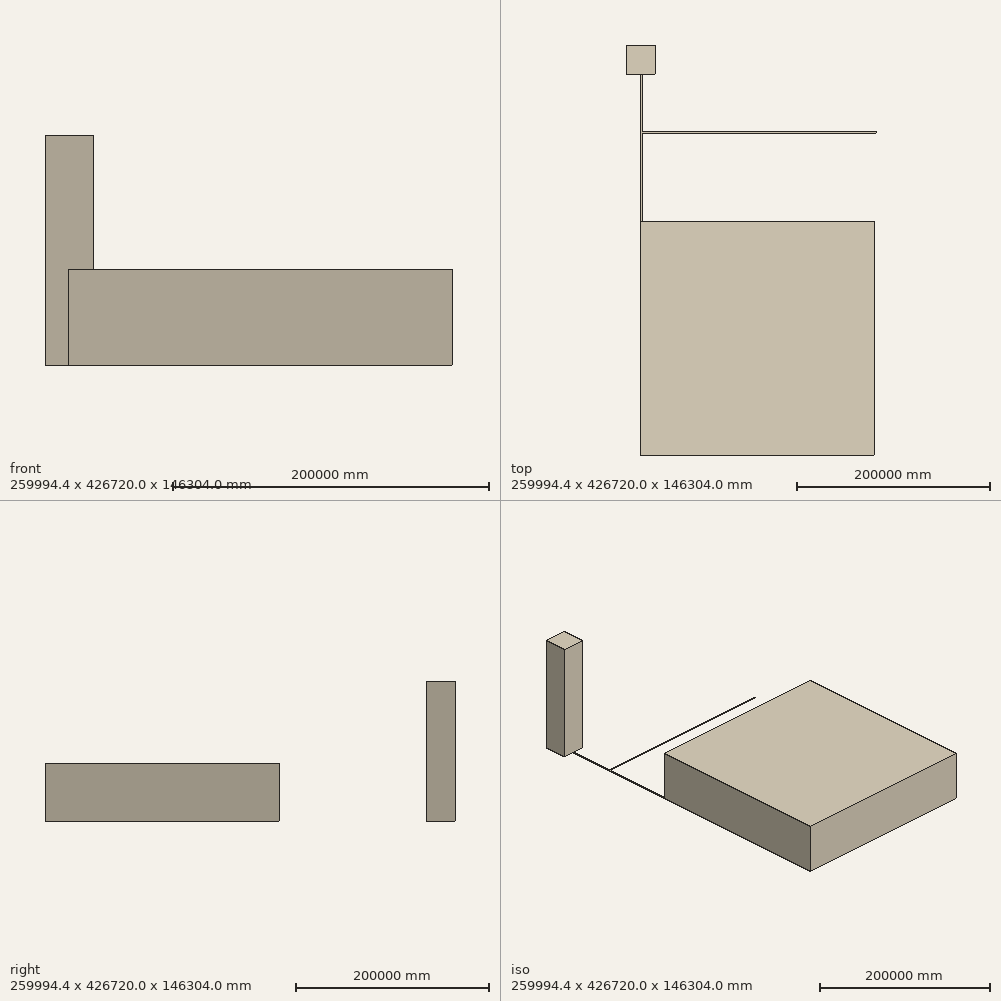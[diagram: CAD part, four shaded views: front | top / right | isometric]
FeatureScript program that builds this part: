
annotation { "Feature Type Name" : "Feature", "Feature Type Description" : "" }
export const myFeature = defineFeature(function(context is Context, id is Id, definition is map)
    precondition{}
    {
        {
            var Q0;
            Q0=qCreatedBy(makeId("Top.planeOp"),FACE);
            var sketch = newSketch(context, id + "F0", { "sketchPlane" : qUnion([Q0])});
            skLineSegment(sketch, "E0.bottom", {"start": v(15240, -15240) * mm, "end": v(-15240, -15240) * mm});
            skLineSegment(sketch, "E0.top", {"start": v(15240, 15240) * mm, "end": v(-15240, 15240) * mm});
            skLineSegment(sketch, "E0.left", {"start": v(15240, -15240) * mm, "end": v(15240, 15240) * mm});
            skLineSegment(sketch, "E0.right", {"start": v(-15240, -15240) * mm, "end": v(-15240, 15240) * mm});
            skPoint(sketch, "E0.middle", {"position": v(0, 0) * mm});
            skLineSegment(sketch, "E1.bottom", {"start": v(-914.4, -15240) * mm, "end": v(914.4, -15240) * mm});
            skLineSegment(sketch, "E1.left", {"start": v(-914.4, -15240) * mm, "end": v(-914.4, -167640) * mm});
            skLineSegment(sketch, "E1.right", {"start": v(914.4, -15240) * mm, "end": v(914.4, -167640) * mm});
            skLineSegment(sketch, "E2.bottom", {"start": v(914.4, -167640) * mm, "end": v(242925.6, -167640) * mm});
            skLineSegment(sketch, "E2.top", {"start": v(-914.4, -411480) * mm, "end": v(242925.6, -411480) * mm});
            skLineSegment(sketch, "E2.left", {"start": v(-914.4, -167640) * mm, "end": v(-914.4, -411480) * mm});
            skLineSegment(sketch, "E2.right", {"start": v(242925.6, -167640) * mm, "end": v(242925.6, -411480) * mm});
            skLineSegment(sketch, "E3", {"start": v(-914.4, -167640) * mm, "end": v(914.4, -167640) * mm});
            skLineSegment(sketch, "E4.bottom", {"start": v(914.4, -74152.27) * mm, "end": v(244754.4, -74152.27) * mm});
            skLineSegment(sketch, "E4.top", {"start": v(914.4, -75981.07) * mm, "end": v(244754.4, -75981.07) * mm});
            skLineSegment(sketch, "E4.left", {"start": v(914.4, -74152.27) * mm, "end": v(914.4, -75981.07) * mm});
            skLineSegment(sketch, "E4.right", {"start": v(244754.4, -74152.27) * mm, "end": v(244754.4, -75981.07) * mm});
            skSolve(sketch);
        }
        {
            var Q0;
            Q0=makeQuery(id+"F0.imprint","IMPRINT",FACE,{"disambiguationData":[TD([[makeQuery(id+"F0.imprint","IMPRINT",EDGE,{"derivedFrom":sQuery(id+"F0.wireOp",EDGE,"E0.top")}),1.0]])]});
            extrude(context, id + "F1", {"entities" : qUnion([Q0]), "depth" : 146304 * mm, "offsetDistance" : 25.4 * mm});
        }
        {
            var Q0;
            {var subQ2=sQuery(id+"F0.wireOp",EDGE,"E4.bottom");Q0=makeQuery(id+"F0.imprint","IMPRINT",FACE,{"disambiguationData":[TD([[makeQuery(id+"F0.imprint","IMPRINT",EDGE,{"derivedFrom":subQ2}),-1.0]])]});}
            var Q1;
            {var subQ4=sQuery(id+"F0.wireOp",EDGE,"E1.left");Q1=makeQuery(id+"F0.imprint","IMPRINT",FACE,{"disambiguationData":[TD([[makeQuery(id+"F0.imprint","IMPRINT",EDGE,{"derivedFrom":subQ4}),1.0]])]});}
            extrude(context, id + "F2", {"entities" : qUnion([Q0, Q1]), "operationType" : NewBodyOperationType.ADD, "depth" : 50.8 * mm, "offsetDistance" : 25.4 * mm});
        }
        {
            var Q0;
            Q0=makeQuery(id+"F0.imprint","IMPRINT",FACE,{"disambiguationData":[TD([[makeQuery(id+"F0.imprint","IMPRINT",EDGE,{"derivedFrom":sQuery(id+"F0.wireOp",EDGE,"E2.bottom")}),-1.0]])]});
            extrude(context, id + "F3", {"entities" : qUnion([Q0]), "operationType" : NewBodyOperationType.ADD, "depth" : 60960 * mm, "offsetDistance" : 25.4 * mm});
        }
        {
            var Q0;
            Q0=makeQuery(id+"F3.opExtrude","SWEPT_FACE",FACE,{"disambiguationData":[OSD([sQuery(id+"F0.wireOp",EDGE,"E2.right")])]});
            shell(context, id + "F4", {"entities" : qUnion([Q0]), "thickness" : 304.8 * mm});
        }
        {
            var Q0;
            Q0=makeQuery(id+"F4.opShell","OFFSET_FACE",FACE,{"disambiguationData":[OSD([sQuery(id+"F0.wireOp",EDGE,"E0.bottom"),sQuery(id+"F0.wireOp",EDGE,"E0.top"),sQuery(id+"F0.wireOp",EDGE,"E0.left"),sQuery(id+"F0.wireOp",EDGE,"E0.right"),sQuery(id+"F0.wireOp",EDGE,"E1.left"),sQuery(id+"F0.wireOp",EDGE,"E1.right"),sQuery(id+"F0.wireOp",EDGE,"E2.bottom"),sQuery(id+"F0.wireOp",EDGE,"E2.top"),sQuery(id+"F0.wireOp",EDGE,"E2.left"),sQuery(id+"F0.wireOp",EDGE,"E2.right"),sQuery(id+"F0.wireOp",EDGE,"E3"),sQuery(id+"F0.wireOp",EDGE,"E4.bottom"),sQuery(id+"F0.wireOp",EDGE,"E4.top"),sQuery(id+"F0.wireOp",EDGE,"E4.right")])]});
            cPlane(context, id + "F5", {"entities" : qUnion([Q0]), "cplaneType" : CPlaneType.OFFSET, "offset" : 0 * mm, "width" : 152.4 * mm, "height" : 152.4 * mm});
        }
    });
